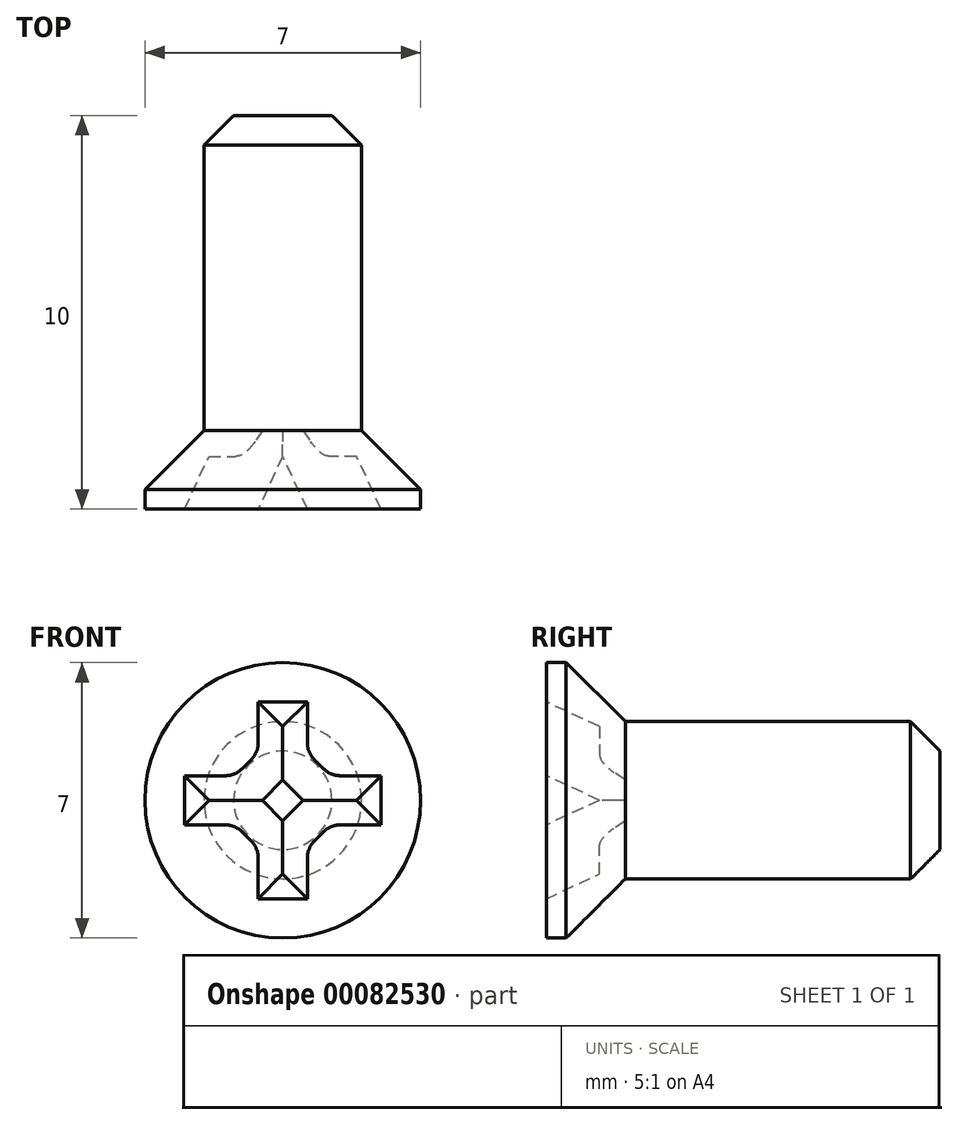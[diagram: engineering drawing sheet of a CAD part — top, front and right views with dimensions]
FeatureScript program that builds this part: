
annotation { "Feature Type Name" : "Feature", "Feature Type Description" : "" }
export const myFeature = defineFeature(function(context is Context, id is Id, definition is map)
    precondition{}
    {
        {
            var Q0;
            Q0=qCreatedBy(makeId("Right.planeOp"),FACE);
            var sketch = newSketch(context, id + "F0", { "sketchPlane" : qUnion([Q0])});
            skLineSegment(sketch, "E0", {"start": v(-4.9, 0) * mm, "end": v(9.48, 0) * mm, "construction": true});
            skLineSegment(sketch, "E1", {"start": v(8, 0) * mm, "end": v(8, 2) * mm});
            skLineSegment(sketch, "E2", {"start": v(8, 2) * mm, "end": v(0, 2) * mm});
            skLineSegment(sketch, "E3", {"start": v(0, 2) * mm, "end": v(-1.5, 3.5) * mm});
            skLineSegment(sketch, "E4", {"start": v(-1.5, 3.5) * mm, "end": v(-2, 3.5) * mm});
            skLineSegment(sketch, "E5", {"start": v(-2, 3.5) * mm, "end": v(-2, 0) * mm});
            skLineSegment(sketch, "E6", {"start": v(-2, 0) * mm, "end": v(8, 0) * mm});
            skSolve(sketch);
        }
        {
            var Q0;
            Q0 = qSketchRegion(id + "F0", true);
            var Q1;
            Q1=sQuery(id+"F0.wireOp",EDGE,"E0");
            revolve(context, id + "F1", {"entities" : qUnion([Q0]), "axis" : qUnion([Q1]), "revolveType" : RevolveType.FULL});
        }
        {
            var Q0;
            Q0=makeQuery(id+"F1.opRevolve","SWEPT_EDGE",EDGE,{"disambiguationData":[OSD([sQuery(id+"F0.wireOp",EDGE,"E1"),sQuery(id+"F0.wireOp",EDGE,"E2")])]});
            chamfer(context, id + "F2", {"entities" : qUnion([Q0]), "width" : 0.75 * mm, "tangentPropagation" : true});
        }
        {
            var Q0;
            Q0=makeQuery(id+"F1.opRevolve","SWEPT_FACE",FACE,{"disambiguationData":[OSD([sQuery(id+"F0.wireOp",EDGE,"E5")])]});
            var sketch = newSketch(context, id + "F3", { "sketchPlane" : qUnion([Q0])});
            skLineSegment(sketch, "E7.bottom", {"start": v(0.62, 2.5) * mm, "end": v(-0.63, 2.5) * mm});
            skLineSegment(sketch, "E7.top", {"start": v(0.63, -2.5) * mm, "end": v(-0.63, -2.5) * mm});
            skLineSegment(sketch, "E7.left", {"start": v(0.62, 2.5) * mm, "end": v(0.63, -2.5) * mm});
            skLineSegment(sketch, "E7.right", {"start": v(-0.63, 2.5) * mm, "end": v(-0.63, -2.5) * mm});
            skPoint(sketch, "E7.middle", {"position": v(0, 0) * mm});
            skLineSegment(sketch, "E8.bottom", {"start": v(2.5, -0.62) * mm, "end": v(-2.5, -0.62) * mm});
            skLineSegment(sketch, "E8.top", {"start": v(2.5, 0.63) * mm, "end": v(-2.5, 0.62) * mm});
            skLineSegment(sketch, "E8.left", {"start": v(2.5, -0.62) * mm, "end": v(2.5, 0.63) * mm});
            skLineSegment(sketch, "E8.right", {"start": v(-2.5, -0.63) * mm, "end": v(-2.5, 0.62) * mm});
            skLineSegment(sketch, "E9.bottom", {"start": v(1.84, 0) * mm, "end": v(0, 1.84) * mm});
            skLineSegment(sketch, "E9.top", {"start": v(0, -1.84) * mm, "end": v(-1.84, 0) * mm});
            skLineSegment(sketch, "E9.left", {"start": v(1.84, 0) * mm, "end": v(0, -1.84) * mm});
            skLineSegment(sketch, "E9.right", {"start": v(0, 1.84) * mm, "end": v(-1.84, 0) * mm});
            skSolve(sketch);
        }
        {
            var Q0;
            Q0=makeQuery(id+"F1.opRevolve","SWEPT_FACE",FACE,{"disambiguationData":[OSD([sQuery(id+"F0.wireOp",EDGE,"E5")])]});
            var sketch = newSketch(context, id + "F4", { "sketchPlane" : qUnion([Q0])});
            skLineSegment(sketch, "E10.0", {"start": v(0.62, 2.5) * mm, "end": v(-0.63, 2.5) * mm});
            skLineSegment(sketch, "E10.1", {"start": v(0.63, -2.5) * mm, "end": v(-0.63, -2.5) * mm});
            skLineSegment(sketch, "E10.2", {"start": v(0.62, 2.5) * mm, "end": v(0.62, 1.21) * mm});
            skLineSegment(sketch, "E10.3", {"start": v(-0.63, 2.5) * mm, "end": v(-0.63, 1.21) * mm});
            skLineSegment(sketch, "E10.5", {"start": v(2.5, -0.62) * mm, "end": v(1.21, -0.62) * mm});
            skLineSegment(sketch, "E10.6", {"start": v(2.5, 0.63) * mm, "end": v(1.21, 0.63) * mm});
            skLineSegment(sketch, "E10.7", {"start": v(2.5, -0.62) * mm, "end": v(2.5, 0.63) * mm});
            skLineSegment(sketch, "E10.8", {"start": v(-2.5, -0.63) * mm, "end": v(-2.5, 0.62) * mm});
            skLineSegment(sketch, "E10.10", {"start": v(1.21, 0.63) * mm, "end": v(0.62, 1.21) * mm});
            skLineSegment(sketch, "E10.11", {"start": v(-0.63, -1.21) * mm, "end": v(-1.21, -0.63) * mm});
            skLineSegment(sketch, "E10.12", {"start": v(1.21, -0.62) * mm, "end": v(0.63, -1.21) * mm});
            skLineSegment(sketch, "E10.13", {"start": v(-0.63, 1.21) * mm, "end": v(-1.21, 0.62) * mm});
            skLineSegment(sketch, "E11.trimOffspring", {"start": v(-1.21, 0.62) * mm, "end": v(-2.5, 0.62) * mm});
            skLineSegment(sketch, "E12.trimOffspring", {"start": v(-0.63, -1.21) * mm, "end": v(-0.63, -2.5) * mm});
            skLineSegment(sketch, "E13.trimOffspring", {"start": v(-1.21, -0.62) * mm, "end": v(-2.5, -0.62) * mm});
            skLineSegment(sketch, "E14.trimOffspring", {"start": v(0.63, -1.21) * mm, "end": v(0.63, -2.5) * mm});
            skSolve(sketch);
        }
        {
            var Q0;
            Q0 = qSketchRegion(id + "F4", true);
            extrude(context, id + "F5", {"entities" : qUnion([Q0]), "operationType" : NewBodyOperationType.REMOVE, "oppositeDirection" : true, "depth" : 2 * mm, "hasDraft" : true, "draftAngle" : 25 * degree, "draftPullDirection" : true});
        }
        {
            var Q0;
            Q0=makeQuery(id+"F5.boolean.opBoolean","COPY",EDGE,{"derivedFrom":makeQuery(id+"F5.opExtrude","SWEPT_EDGE",EDGE,{"disambiguationData":[OSD([sQuery(id+"F4.wireOp",EDGE,"E10.3"),sQuery(id+"F4.wireOp",EDGE,"E10.13")])]})});
            var Q1;
            Q1=makeQuery(id+"F5.boolean.opBoolean","COPY",EDGE,{"derivedFrom":makeQuery(id+"F5.opExtrude","SWEPT_EDGE",EDGE,{"disambiguationData":[OSD([sQuery(id+"F4.wireOp",EDGE,"E10.13"),sQuery(id+"F4.wireOp",EDGE,"E11.trimOffspring")])]})});
            var Q2;
            Q2=makeQuery(id+"F5.boolean.opBoolean","COPY",EDGE,{"derivedFrom":makeQuery(id+"F5.opExtrude","SWEPT_EDGE",EDGE,{"disambiguationData":[OSD([sQuery(id+"F4.wireOp",EDGE,"E10.2"),sQuery(id+"F4.wireOp",EDGE,"E10.10")])]})});
            var Q3;
            Q3=makeQuery(id+"F5.boolean.opBoolean","COPY",EDGE,{"derivedFrom":makeQuery(id+"F5.opExtrude","SWEPT_EDGE",EDGE,{"disambiguationData":[OSD([sQuery(id+"F4.wireOp",EDGE,"E10.6"),sQuery(id+"F4.wireOp",EDGE,"E10.10")])]})});
            var Q4;
            Q4=makeQuery(id+"F5.boolean.opBoolean","COPY",EDGE,{"derivedFrom":makeQuery(id+"F5.opExtrude","SWEPT_EDGE",EDGE,{"disambiguationData":[OSD([sQuery(id+"F4.wireOp",EDGE,"E10.5"),sQuery(id+"F4.wireOp",EDGE,"E10.12")])]})});
            var Q5;
            Q5=makeQuery(id+"F5.boolean.opBoolean","COPY",EDGE,{"derivedFrom":makeQuery(id+"F5.opExtrude","SWEPT_EDGE",EDGE,{"disambiguationData":[OSD([sQuery(id+"F4.wireOp",EDGE,"E10.12"),sQuery(id+"F4.wireOp",EDGE,"E14.trimOffspring")])]})});
            var Q6;
            Q6=makeQuery(id+"F5.boolean.opBoolean","COPY",EDGE,{"derivedFrom":makeQuery(id+"F5.opExtrude","SWEPT_EDGE",EDGE,{"disambiguationData":[OSD([sQuery(id+"F4.wireOp",EDGE,"E10.11"),sQuery(id+"F4.wireOp",EDGE,"E13.trimOffspring")])]})});
            var Q7;
            Q7=makeQuery(id+"F5.boolean.opBoolean","COPY",EDGE,{"derivedFrom":makeQuery(id+"F5.opExtrude","SWEPT_EDGE",EDGE,{"disambiguationData":[OSD([sQuery(id+"F4.wireOp",EDGE,"E10.11"),sQuery(id+"F4.wireOp",EDGE,"E12.trimOffspring")])]})});
            fillet(context, id + "F6", {"entities" : qUnion([Q0, Q1, Q2, Q3, Q4, Q5, Q6, Q7]), "radius" : 0.65 * mm, "tangentPropagation" : true, "allowEdgeOverflow" : false});
        }
    });
